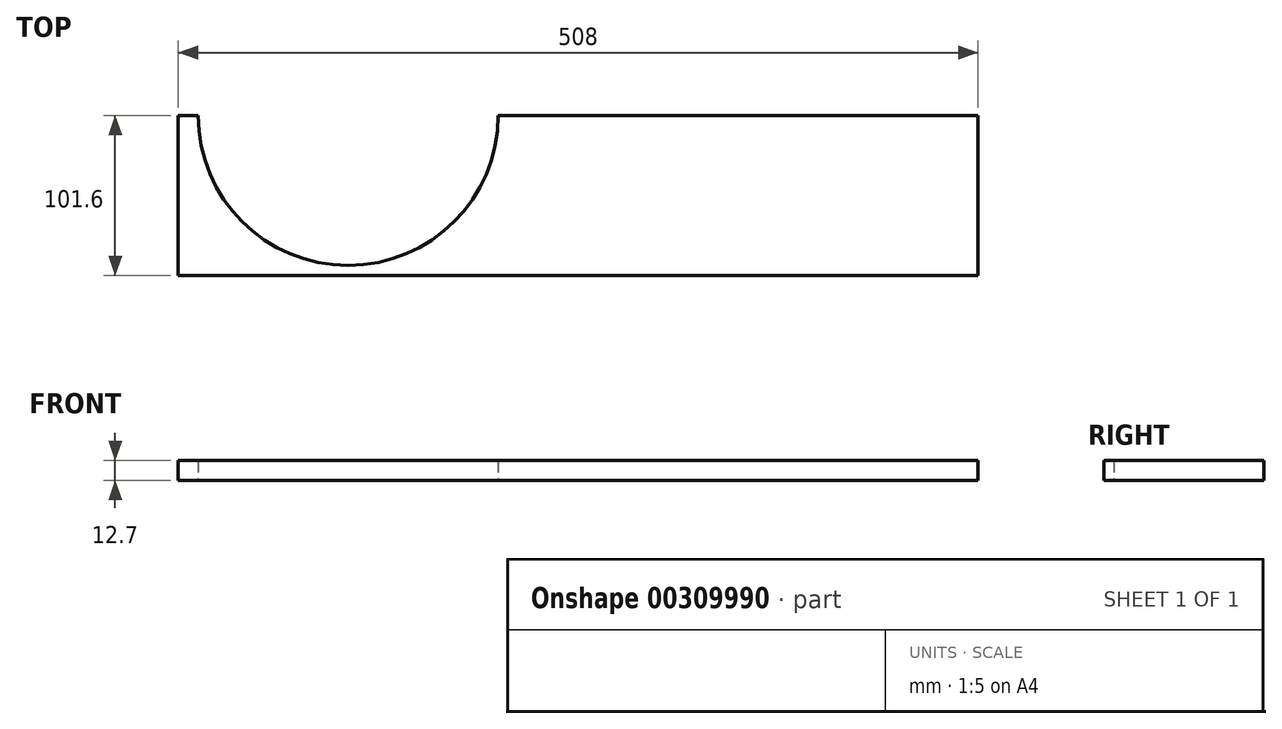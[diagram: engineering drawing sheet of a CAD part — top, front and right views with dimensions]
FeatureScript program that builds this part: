
annotation { "Feature Type Name" : "Feature", "Feature Type Description" : "" }
export const myFeature = defineFeature(function(context is Context, id is Id, definition is map)
    precondition{}
    {
        {
            var Q0;
            Q0=qCreatedBy(makeId("Top.planeOp"),FACE);
            var sketch = newSketch(context, id + "F0", { "sketchPlane" : qUnion([Q0])});
            skLineSegment(sketch, "E0.bottom", {"start": v(-254, 50.8) * mm, "end": v(-241.3, 50.8) * mm});
            skLineSegment(sketch, "E0.top", {"start": v(-254, -50.8) * mm, "end": v(254, -50.8) * mm});
            skLineSegment(sketch, "E0.left", {"start": v(-254, 50.8) * mm, "end": v(-254, -50.8) * mm});
            skLineSegment(sketch, "E0.right", {"start": v(254, 50.8) * mm, "end": v(254, -50.8) * mm});
            skPoint(sketch, "E0.middle", {"position": v(0, 0) * mm});
            skArc(sketch, "E1", {"start": v(-241.3, 50.8) * mm, "mid": v(-146.05, -44.45) * mm, "end": v(-50.8, 50.8) * mm});
            skLineSegment(sketch, "E2.trimOffspring", {"start": v(-50.8, 50.8) * mm, "end": v(254, 50.8) * mm});
            skSolve(sketch);
        }
        {
            var Q0;
            Q0 = qSketchRegion(id + "F0", true);
            extrude(context, id + "F1", {"entities" : qUnion([Q0]), "depth" : 12.7 * mm});
        }
    });
